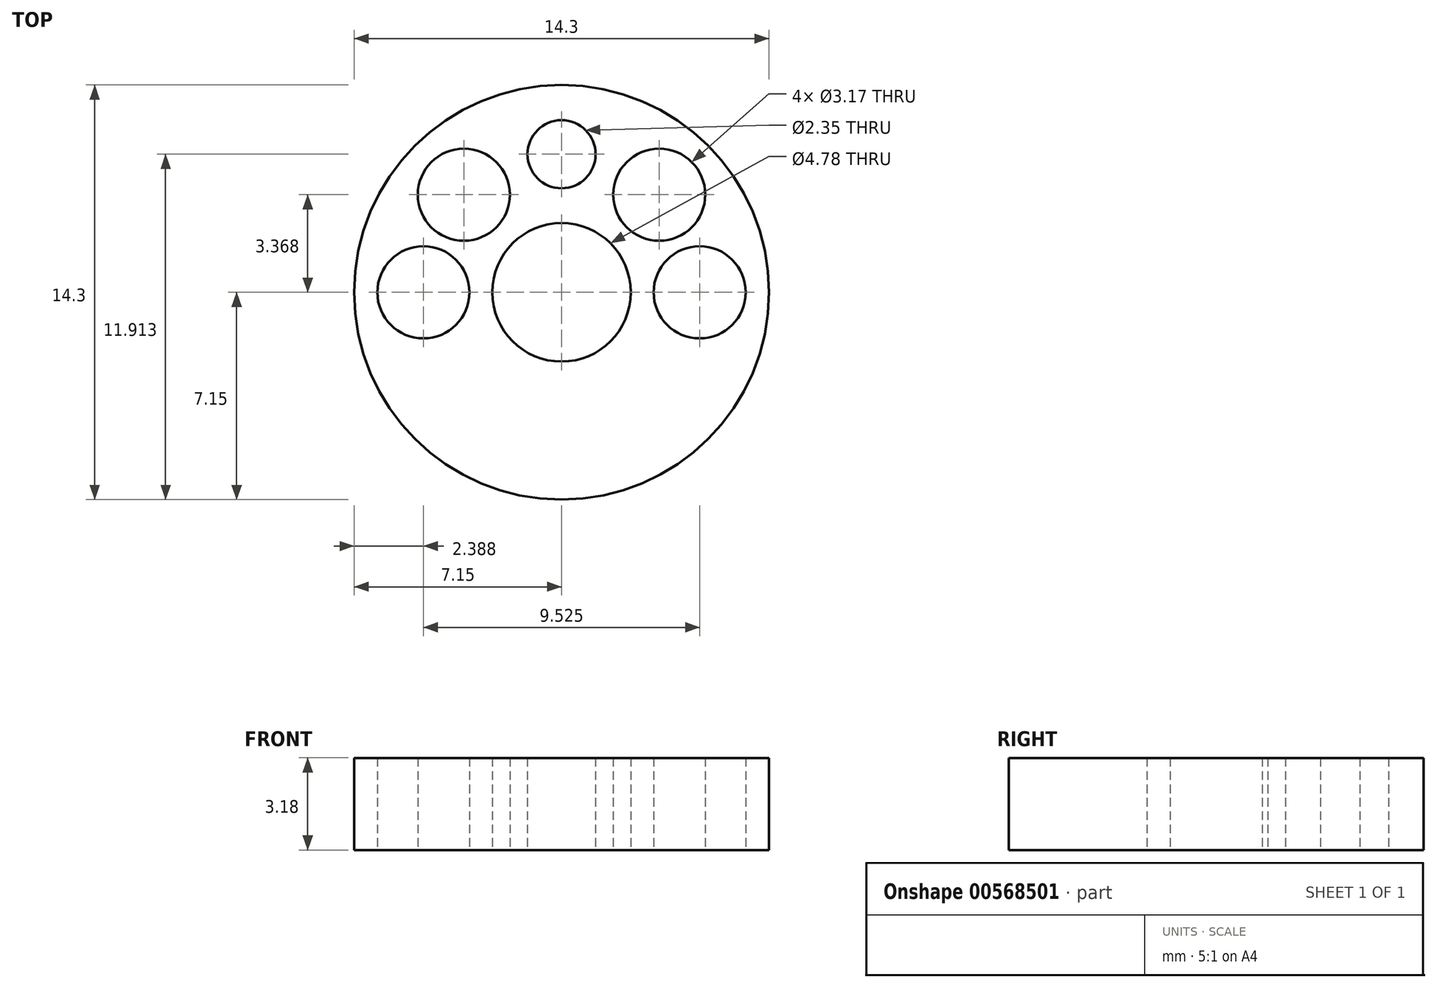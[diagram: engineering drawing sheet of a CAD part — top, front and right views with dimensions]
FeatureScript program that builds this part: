
annotation { "Feature Type Name" : "Feature", "Feature Type Description" : "" }
export const myFeature = defineFeature(function(context is Context, id is Id, definition is map)
    precondition{}
    {
        {
            var Q0;
            Q0=qCreatedBy(makeId("Top.planeOp"),FACE);
            var sketch = newSketch(context, id + "F0", { "sketchPlane" : qUnion([Q0])});
            skCircle(sketch, "E0", {"center": v(0, 0) * mm, "radius": 7.15 * mm});
            skCircle(sketch, "E1", {"center": v(0, 0) * mm, "radius": 2.39 * mm});
            skCircle(sketch, "E2", {"center": v(0, 0) * mm, "radius": 4.76 * mm});
            skCircle(sketch, "E3", {"center": v(-4.76, 0) * mm, "radius": 1.59 * mm});
            skCircle(sketch, "E4.4.0", {"center": v(4.76, 0) * mm, "radius": 1.59 * mm});
            skCircle(sketch, "E4.5.0", {"center": v(3.37, 3.37) * mm, "radius": 1.59 * mm});
            skCircle(sketch, "E4.7.0", {"center": v(-3.37, 3.37) * mm, "radius": 1.59 * mm});
            skCircle(sketch, "E5", {"center": v(0, 4.76) * mm, "radius": 1.17 * mm});
            skSolve(sketch);
        }
        {
            var Q0;
            Q0 = qSketchRegion(id + "F0", true);
            var Q1;
            Q1=makeQuery(id+"F0.imprint","IMPRINT",FACE,{"disambiguationData":[TD([[makeQuery(id+"F0.imprint","IMPRINT",EDGE,{"derivedFrom":sQuery(id+"F0.wireOp",EDGE,"E1")}),-1.0]])]});
            extrude(context, id + "F1", {"entities" : qUnion([Q0, Q1]), "depth" : 3.17 * mm, "offsetDistance" : 25.4 * mm});
        }
    });
